# Revit family: 0044133 Feilo Sylvania Lighting Fixture OPTIX R 600 2L 4K WHT DA
name_source: partatom
category: Lighting Fixtures
revit_build: Autodesk Revit 2017 (Build: 20190507_1515(x64)
units: mm (PartAtom-declared; Revit-internal decimal feet)

## family parameters
Cut with Voids When Loaded = No
Host = Face
Light Source = No
OmniClass Number = 23.80.70.00
OmniClass Title = Lighting
Part Type = Normal
Room Calculation Point = No
Round Connector Dimension = Use Diameter
Shared = No

## types (1)
- 0044133 OPTIX R 600 2L 4K WHT DA
    Apparent Load = 23 VA
    Assembly Code = D5020200
    AssetType = Fixed
    ClassificationName = Uniclass2015
    ClassificationValue = EF_70_80
    Cost = 0 $
    Default Elevation = 1219 mm
    Description = OPTIX RECESSED 600x600 2L 4000K WHITE DALI is a high efficacy low glare luminaire for office and education applications. Ceiling recessed 600x600 mm. White plastic low glare optics in 2 lines configuration. White RAL9016 fixture body. DALI dimmable. 4000K Neutral White LED, CRI>80, chromaticity tolerance of 3-step MacAdam ellipse. Luminous flux 3350lm. Power consumption 23W. Luminaire efficacy 146lm/W. Lumen maintenance of L90B50 > 72000h, L90B10 = 46000h. UGR<19, IK07, IP20. Photobiological safety risk group 1. Electrical protection Class I. Glow wire test 650°C.
    DimmingControlOptions = Dimmable
    DocumentationLiterature = http://www.sylvania-lighting.com
    DurationUnit = hours
    ElectricShockClassification = Class I
    ExpectedLife = 50000
    Height = 38 mm  [stored 0.124672 ft]
    IfcExportAs = IfcLightFixtureType
    IfcExportType = IfcLightFixtureType
    ImpactProtectionIndex = IK07
    IngressProtection = IP20
    InputNominalFrequency = 50/60 Hz
    InputVoltage = 220-240V~
    Keynote = 16500
    Lamp = LED
    LampColourRenderingIndex = 80
    LampColourTemperature = 4000 K
    LampMacAdamStep = 3
    LampNominalLuminous = 3350 lm
    LampsType = LED
    Length = 596 mm  [stored 1.95538 ft]
    LuminousEfficacy = 146 lm/W
    Manufacturer = Feilo Sylvania
    ManufacturerName = Feilo Sylvania
    Material = steel housing, polycarbonate diffuser
    Material_1_FEILO = <By Category>
    Material_2_FEILO = <By Category>
    Material_3_FEILO = <By Category>
    Material_4_FEILO = <By Category>
    Model = OPTIX R 600 2L 4K WHT DA
    ModelNumber = 0044133
    ModelReference = OPTIX R 600 2L 4K WHT DA
    Name = OPTIX R 600 2L 4K WHT DA
    NominalDepth = 596 mm  [stored 1.95538 ft]
    NominalHeight = 38 mm  [stored 0.124672 ft]
    NominalLength = 596 mm  [stored 1.95538 ft]
    PowerConsumption = 23 W
    PowerFactor = 0.98
    Type Image = <None>
    TypeName = OPTIX R 600 2L 4K WHT DA
    URL = http://www.sylvania-lighting.com
    Voltage = 230 V
    Weight = 5.0 kg
    Width = 596 mm  [stored 1.95538 ft]

note: [stored X ft] marks values corroborated as IEEE doubles in the binary element streams (Revit-internal decimal feet)

## geometry (parser evidence)
native form markers: Sweep x6
no freeform markers — native parametric forms only
